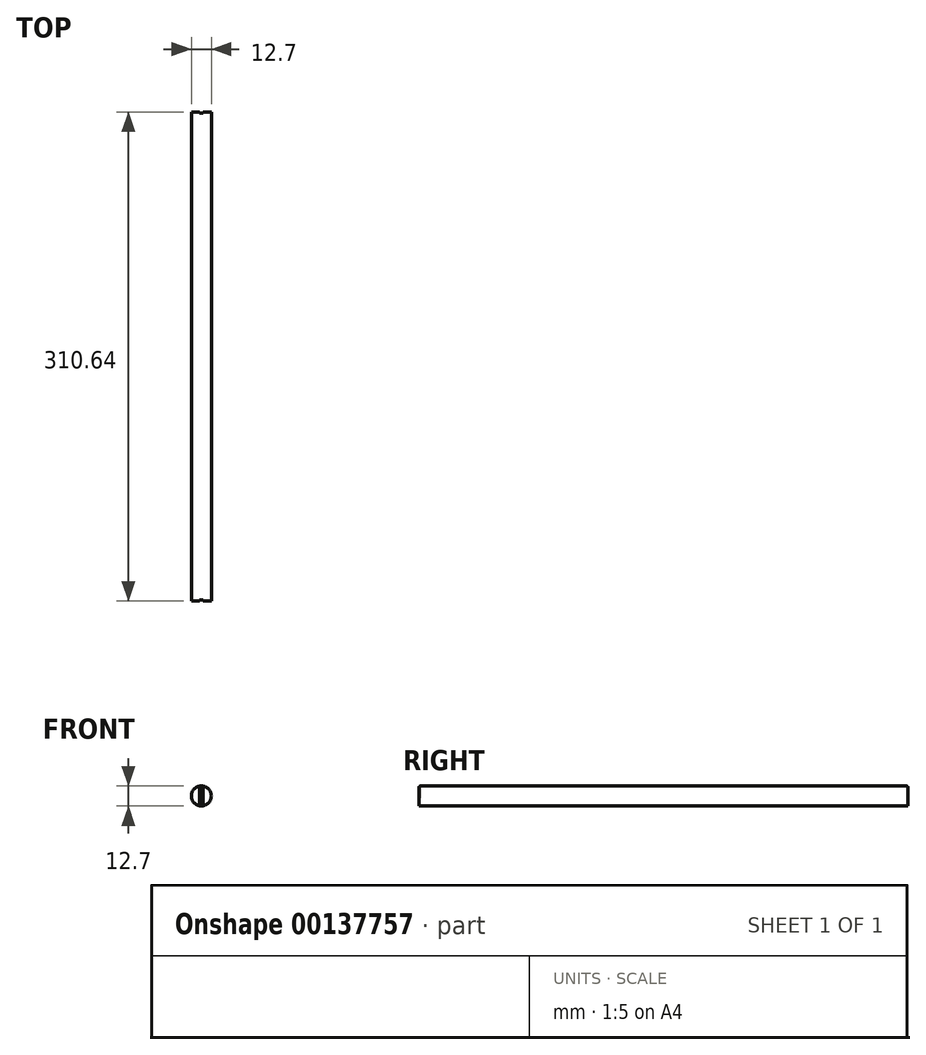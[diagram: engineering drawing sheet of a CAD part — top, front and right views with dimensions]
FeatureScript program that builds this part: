
annotation { "Feature Type Name" : "Feature", "Feature Type Description" : "" }
export const myFeature = defineFeature(function(context is Context, id is Id, definition is map)
    precondition{}
    {
        {
            var Q0;
            Q0=qCreatedBy(makeId("Front.planeOp"),FACE);
            var sketch = newSketch(context, id + "F0", { "sketchPlane" : qUnion([Q0])});
            skCircle(sketch, "E0", {"center": v(0, 0) * mm, "radius": 6.35 * mm});
            skSolve(sketch);
        }
        {
            var Q0;
            Q0=makeQuery(id+"F0.imprint","IMPRINT",FACE,{"disambiguationData":[TD([[makeQuery(id+"F0.imprint","IMPRINT",EDGE,{"derivedFrom":sQuery(id+"F0.wireOp",EDGE,"E0")}),1.0]])]});
            var Q1;
            Q1=sQuery(id+"F0.wireOp",EDGE,"E0");
            extrude(context, id + "F1", {"entities" : qUnion([Q0]), "surfaceEntities" : qUnion([Q1]), "endBound" : BoundingType.SYMMETRIC, "oppositeDirection" : true, "depth" : 310.64 * mm});
        }
        {
            var Q0;
            Q0=makeQuery(id+"F1.opExtrude","CAP_FACE",FACE,{"disambiguationData":[OSD([sQuery(id+"F0.wireOp",EDGE,"E0")])],"isStart":true});
            var sketch = newSketch(context, id + "F2", { "sketchPlane" : qUnion([Q0])});
            skLineSegment(sketch, "E1.bottom", {"start": v(-1.14, 6.35) * mm, "end": v(1.14, 6.35) * mm});
            skLineSegment(sketch, "E1.top", {"start": v(-1.14, -6.35) * mm, "end": v(1.14, -6.35) * mm});
            skLineSegment(sketch, "E1.left", {"start": v(-1.14, 6.35) * mm, "end": v(-1.14, -6.35) * mm});
            skLineSegment(sketch, "E1.right", {"start": v(1.14, 6.35) * mm, "end": v(1.14, -6.35) * mm});
            skLineSegment(sketch, "E2", {"start": v(0, 6.35) * mm, "end": v(0, -6.35) * mm, "construction": true});
            skPoint(sketch, "E2.startSnap0", {"position": v(0, 6.35) * mm});
            skSolve(sketch);
        }
        {
            var Q0;
            Q0 = qSketchRegion(id + "F2", true);
            extrude(context, id + "F3", {"entities" : qUnion([Q0]), "operationType" : NewBodyOperationType.REMOVE, "oppositeDirection" : true, "depth" : 0.76 * mm});
        }
        {
            var Q0;
            Q0=makeQuery(id+"F1.opExtrude","CAP_FACE",FACE,{"disambiguationData":[OSD([sQuery(id+"F0.wireOp",EDGE,"E0")])],"isStart":false});
            var sketch = newSketch(context, id + "F4", { "sketchPlane" : qUnion([Q0])});
            skLineSegment(sketch, "E3.0", {"start": v(-1.14, 6.35) * mm, "end": v(-1.14, -6.35) * mm});
            skLineSegment(sketch, "E3.1", {"start": v(1.14, 6.35) * mm, "end": v(1.14, -6.35) * mm});
            skLineSegment(sketch, "E3.2", {"start": v(1.14, 6.35) * mm, "end": v(-1.14, 6.35) * mm});
            skLineSegment(sketch, "E4.0", {"start": v(1.14, -6.35) * mm, "end": v(-1.14, -6.35) * mm});
            skSolve(sketch);
        }
        {
            var Q0;
            Q0 = qSketchRegion(id + "F4", true);
            extrude(context, id + "F5", {"entities" : qUnion([Q0]), "operationType" : NewBodyOperationType.REMOVE, "oppositeDirection" : true, "depth" : 0.76 * mm});
        }
    });
